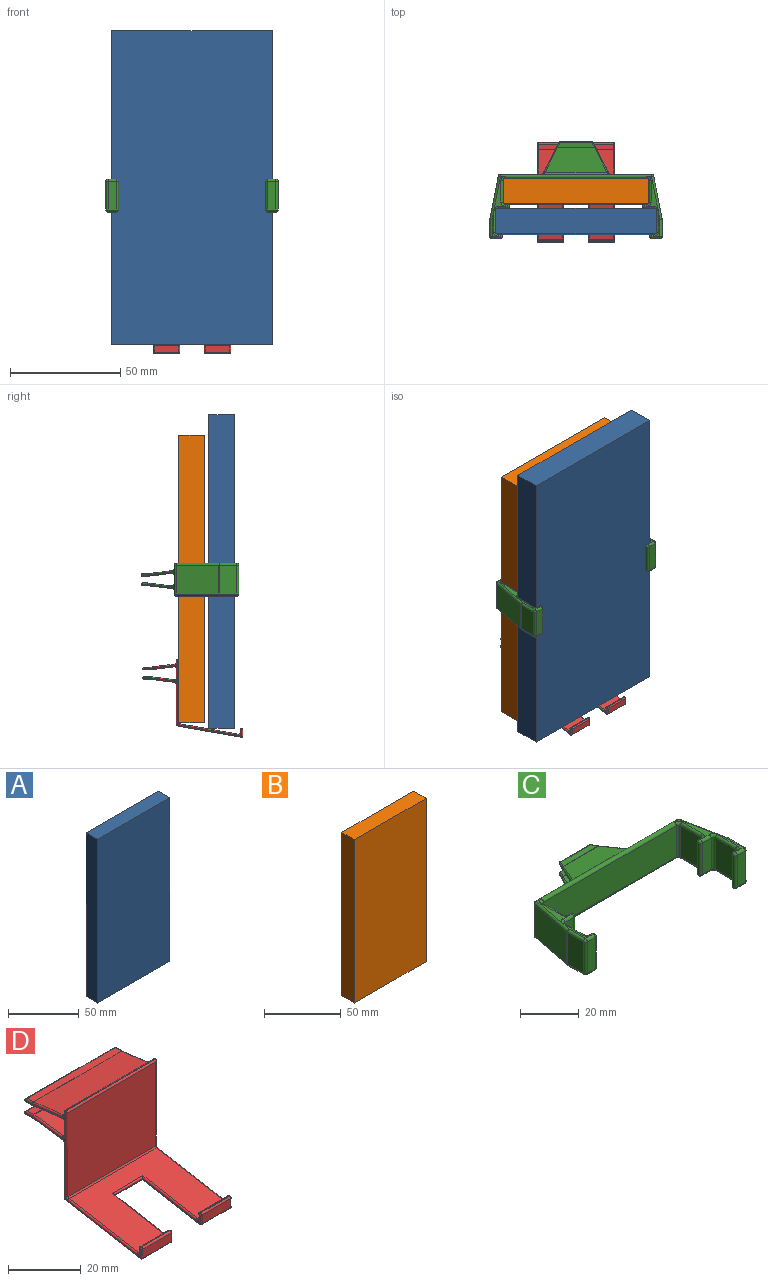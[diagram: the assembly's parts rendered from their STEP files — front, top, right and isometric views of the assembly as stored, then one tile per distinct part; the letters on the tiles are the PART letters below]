
ASSEMBLY  parts=4 mates=3
PART A: 6 faces, bbox 72.5x11.6x142 mm
  f0: plane 72.5x11.6mm, normal (0,0,-1), area 841mm2, adj f1,f3,f4,f5
  f1: plane 142x11.6mm, normal (1,0,0), area 1647.2mm2, adj f0,f2,f4,f5
  f2: plane 72.5x11.6mm, normal (0,0,1), area 841mm2, adj f1,f3,f4,f5
  f3: plane 142x11.6mm, normal (-1,0,0), area 1647.2mm2, adj f0,f2,f4,f5
  f4: plane 142x72.5mm, normal (0,1,0), area 10295mm2, adj f0,f1,f2,f3
  f5: plane 142x72.5mm, normal (0,-1,0), area 10295mm2, adj f0,f1,f2,f3
PART B: 6 faces, bbox 66x11.6x130 mm
  f0: plane 66x11.6mm, normal (0,0,-1), area 765.6mm2, adj f1,f3,f4,f5
  f1: plane 130x11.6mm, normal (1,0,0), area 1508mm2, adj f0,f2,f4,f5
  f2: plane 66x11.6mm, normal (0,0,1), area 765.6mm2, adj f1,f3,f4,f5
  f3: plane 130x11.6mm, normal (-1,0,0), area 1508mm2, adj f0,f2,f4,f5
  f4: plane 130x66mm, normal (0,1,0), area 8580mm2, adj f0,f1,f2,f3
  f5: plane 130x66mm, normal (0,-1,0), area 8580mm2, adj f0,f1,f2,f3
PART C: 188 faces, bbox 78x44.2x15 mm
  f0: plane 11.6x2.75mm, normal (0,0,-1), area 8.1mm2, adj f42,f49,f50,f56,f67
  f1: plane 14.84x5.1mm, normal (0,0,-1), area 22.8mm2, adj f52,f55,f63,f67,f72,f80,f86
  f2: plane 14.84x5.1mm, normal (0,0,-1), area 22.8mm2, adj f86,f91,f99,f100,f101,f106,f112
  f3: plane 11.6x2.75mm, normal (0,0,1), area 8.1mm2, adj f46,f59,f60,f69,f78
  f4: plane 14.84x5.1mm, normal (0,0,1), area 22.8mm2, adj f62,f70,f78,f79,f89,f97,f98
  f5: plane 14.84x5.1mm, normal (0,0,1), area 22.8mm2, adj f97,f110,f111,f115,f116,f118,f119
  f6: plane 14.38x0.2mm, normal (0,1,0), area 2.9mm2, adj f140,f141,f148,f149
  f7: plane 14.38x0.2mm, normal (0,1,0), area 2.9mm2, adj f170,f171,f176,f177
  f8: plane 19.41x13mm, normal (-0.98,0.19,0), area 257.2mm2, adj f91,f95,f96,f110
  f9: plane 13x3.75mm, normal (0,-1,0), area 48.7mm2, adj f65,f66,f75,f83
  f10: plane 11.6x2.75mm, normal (0,0,1), area 8.1mm2, adj f83,f94,f102,f109,f110
  f11: plane 11.6x2.75mm, normal (0,0,-1), area 8.1mm2, adj f65,f81,f82,f91,f92
  f12: plane 27.7x10.85mm, normal (0,-0.12,-0.99), area 243.4mm2, adj f120,f130,f135,f136
  f13: plane 16.85x2.47mm, normal (0,0,-1), area 38.6mm2, adj f134,f135,f141,f142
  f14: plane 16.78x2.39mm, normal (0,0,1), area 37.3mm2, adj f147,f148,f152,f153
  f15: plane 28.07x11.17mm, normal (0,0.12,0.99), area 253.1mm2, adj f123,f146,f152,f155
  f16: plane 16.85x2.47mm, normal (0,0,1), area 38.6mm2, adj f165,f166,f169,f170
  f17: plane 27.7x10.85mm, normal (0,-0.12,0.99), area 243.4mm2, adj f127,f161,f164,f165
  f18: plane 28.07x11.17mm, normal (0,0.12,-0.99), area 253.1mm2, adj f124,f179,f183,f185
  f19: plane 16.78x2.39mm, normal (0,0,-1), area 37.3mm2, adj f177,f178,f182,f183
  f20: plane 68.36x13mm, normal (0,1,0), area 687.2mm2, adj f77,f86,f96,f97,f120,f121,f122,f123
  f21: plane 13x4.25mm, normal (0,-1,0), area 55.2mm2, adj f100,f108,f113,f118
  f22: plane 13x1mm, normal (0,1,0), area 13mm2, adj f100,f113,f117,f118
  f23: plane 13x9.6mm, normal (1,0,0), area 124.8mm2, adj f105,f106,f116,f117
  f24: plane 64x13mm, normal (0,-1,0), area 832mm2, adj f86,f90,f97,f105
  f25: plane 13x9.6mm, normal (-1,0,0), area 124.8mm2, adj f71,f72,f89,f90
  f26: plane 13x1mm, normal (0,1,0), area 13mm2, adj f48,f52,f62,f71
  f27: plane 13x4.25mm, normal (0,-1,0), area 55.2mm2, adj f48,f52,f61,f62
  f28: plane 13x9.6mm, normal (-1,0,0), area 124.8mm2, adj f54,f56,f61,f69
  f29: plane 13x1mm, normal (0,1,0), area 13mm2, adj f41,f42,f46,f54
  f30: plane 13x3.75mm, normal (0,-1,0), area 48.7mm2, adj f41,f42,f45,f46
  f31: plane 19.41x13mm, normal (0.98,0.19,0), area 257.2mm2, adj f58,f67,f77,f78
  f32: plane 13x1mm, normal (0,1,0), area 13mm2, adj f65,f66,f83,f93
  f33: plane 13x9.6mm, normal (1,0,0), area 124.8mm2, adj f92,f93,f108,f109
  f34: plane 14.17x7.09mm, normal (0.89,0.45,0), area 3.3mm2, adj f125,f162,f164,f169,f176,f182,f184,f185
  f35: plane 14.17x7.09mm, normal (-0.89,0.45,0), area 3.3mm2, adj f126,f159,f161,f166,f171,f175,f178,f179
  f36: plane 14.17x7.09mm, normal (0.89,0.45,0), area 3.3mm2, adj f121,f133,f136,f142,f149,f153,f154,f155
  f37: plane 14.17x7.09mm, normal (-0.89,0.45,0), area 3.3mm2, adj f122,f129,f130,f134,f140,f143,f146,f147
  f38: plane 13x7.79mm, normal (-1,0,0), area 101.3mm2, adj f75,f81,f94,f95
  f39: plane 13x7.79mm, normal (1,0,0), area 101.3mm2, adj f45,f50,f58,f59
  f40: sphere r=1mm, area 3.1mm2, adj f41,f42
  f41: cylinder r=1mm len=13mm, axis (0,0,-1), area 40.8mm2, adj f29,f30,f40,f43
  f42: cylinder r=1mm len=3.75mm, axis (1,0,0), area 7.5mm2, adj f0,f29,f30,f40,f44,f49
  f43: sphere r=1mm, area 3.1mm2, adj f41,f46
  f44: sphere r=1mm, area 1.6mm2, adj f42,f45,f50
  f45: cylinder r=1mm len=13mm, axis (0,0,1), area 20.4mm2, adj f30,f39,f44,f51
  f46: cylinder r=1mm len=3.75mm, axis (-1,0,0), area 7.5mm2, adj f3,f29,f30,f43,f51,f60
  f47: sphere r=1mm, area 3.1mm2, adj f48,f52
  f48: cylinder r=1mm len=13mm, axis (0,0,-1), area 40.8mm2, adj f26,f27,f47,f53
  f49: torus R=2mm, axis (0,0,1), area 3.4mm2, adj f0,f42,f54,f56
  f50: cylinder r=1mm len=7.79mm, axis (0,-1,0), area 12.2mm2, adj f0,f39,f44,f57
  f51: sphere r=1mm, area 1.6mm2, adj f45,f46,f59
  f52: cylinder r=1mm len=4.25mm, axis (1,0,0), area 8.2mm2, adj f1,f26,f27,f47,f55,f63
  f53: sphere r=1mm, area 3.1mm2, adj f48,f62
  f54: cylinder r=1mm len=13mm, axis (0,0,1), area 20.4mm2, adj f28,f29,f49,f60
  f55: torus R=2mm, axis (0,0,1), area 3.4mm2, adj f1,f52,f56,f61,f67
  f56: cylinder r=1mm len=9.6mm, axis (0,-1,0), area 15.1mm2, adj f0,f28,f49,f55,f67
  f57: sphere r=1mm, area 0.2mm2, adj f50,f58,f67
  f58: cylinder r=1mm len=13mm, axis (0,0,-1), area 2.5mm2, adj f31,f39,f57,f68
  f59: cylinder r=1mm len=7.79mm, axis (0,1,0), area 12.2mm2, adj f3,f39,f51,f68
  f60: torus R=2mm, axis (0,0,1), area 3.4mm2, adj f3,f46,f54,f69
  f61: cylinder r=1mm len=13mm, axis (0,0,1), area 20.4mm2, adj f27,f28,f55,f70
  f62: cylinder r=1mm len=4.25mm, axis (-1,0,0), area 8.2mm2, adj f4,f26,f27,f53,f70,f79
  f63: torus R=2mm, axis (0,0,1), area 3.4mm2, adj f1,f52,f71,f72
  f64: sphere r=1mm, area 3.1mm2, adj f65,f66
  f65: cylinder r=1mm len=3.75mm, axis (1,0,0), area 7.5mm2, adj f9,f11,f32,f64,f73,f82
  f66: cylinder r=1mm len=13mm, axis (0,0,-1), area 40.8mm2, adj f9,f32,f64,f74
  f67: cylinder r=1mm len=19.6mm, axis (-0.19,0.98,0), area 31.1mm2, adj f0,f1,f31,f55,f56,f57,f76
  f68: sphere r=1mm, area 0.2mm2, adj f58,f59,f78
  f69: cylinder r=1mm len=9.6mm, axis (0,1,0), area 15.1mm2, adj f3,f28,f60,f70,f78
  f70: torus R=2mm, axis (0,0,1), area 3.4mm2, adj f4,f61,f62,f69,f78
  f71: cylinder r=1mm len=13mm, axis (0,0,1), area 20.4mm2, adj f25,f26,f63,f79
  f72: cylinder r=1mm len=9.6mm, axis (0,-1,0), area 15.1mm2, adj f1,f25,f63,f80
  f73: sphere r=1mm, area 1.6mm2, adj f65,f75,f81
  f74: sphere r=1mm, area 3.1mm2, adj f66,f83
  f75: cylinder r=1mm len=13mm, axis (0,0,-1), area 20.4mm2, adj f9,f38,f73,f84
  f76: sphere r=1mm, area 1.4mm2, adj f67,f77,f86
  f77: cylinder r=1mm len=13mm, axis (0,0,1), area 17.9mm2, adj f20,f31,f76,f88
  f78: cylinder r=1mm len=19.6mm, axis (0.19,-0.98,0), area 31.1mm2, adj f3,f4,f31,f68,f69,f70,f88
  f79: torus R=2mm, axis (0,0,1), area 3.4mm2, adj f4,f62,f71,f89
  f80: torus R=2mm, axis (0,0,1), area 3.4mm2, adj f1,f72,f86,f90
  f81: cylinder r=1mm len=7.79mm, axis (0,1,0), area 12.2mm2, adj f11,f38,f73,f85
  f82: torus R=2mm, axis (0,0,1), area 3.4mm2, adj f11,f65,f92,f93
  f83: cylinder r=1mm len=3.75mm, axis (-1,0,0), area 7.5mm2, adj f9,f10,f32,f74,f84,f102
  f84: sphere r=1mm, area 1.6mm2, adj f75,f83,f94
  f85: sphere r=1mm, area 0.2mm2, adj f81,f91,f95
  f86: cylinder r=1mm len=68.36mm, axis (-1,0,0), area 207.9mm2, adj f1,f2,f20,f24,f76,f80,f87,f99
  f87: sphere r=1mm, area 1.4mm2, adj f86,f91,f96
  f88: sphere r=1mm, area 1.4mm2, adj f77,f78,f97
  f89: cylinder r=1mm len=9.6mm, axis (0,1,0), area 15.1mm2, adj f4,f25,f79,f98
  f90: cylinder r=1mm len=13mm, axis (0,0,-1), area 20.4mm2, adj f24,f25,f80,f98
  f91: cylinder r=1mm len=19.6mm, axis (-0.19,-0.98,0), area 31.1mm2, adj f2,f8,f11,f85,f87,f92,f101
  f92: cylinder r=1mm len=9.6mm, axis (0,1,0), area 15.1mm2, adj f11,f33,f82,f91,f101
  f93: cylinder r=1mm len=13mm, axis (0,0,1), area 20.4mm2, adj f32,f33,f82,f102
  f94: cylinder r=1mm len=7.79mm, axis (0,-1,0), area 12.2mm2, adj f10,f38,f84,f103
  f95: cylinder r=1mm len=13mm, axis (0,0,1), area 2.5mm2, adj f8,f38,f85,f103
  f96: cylinder r=1mm len=13mm, axis (0,0,-1), area 17.9mm2, adj f8,f20,f87,f104
  f97: cylinder r=1mm len=68.36mm, axis (1,0,0), area 207.9mm2, adj f4,f5,f20,f24,f88,f98,f104,f111
  f98: torus R=2mm, axis (0,0,1), area 3.4mm2, adj f4,f89,f90,f97
  f99: torus R=2mm, axis (0,0,1), area 3.4mm2, adj f2,f86,f105,f106
  f100: cylinder r=1mm len=4.25mm, axis (1,0,0), area 8.2mm2, adj f2,f21,f22,f101,f107,f112
  f101: torus R=2mm, axis (0,0,1), area 3.4mm2, adj f2,f91,f92,f100,f108
  f102: torus R=2mm, axis (0,0,1), area 3.4mm2, adj f10,f83,f93,f109
  f103: sphere r=1mm, area 0.2mm2, adj f94,f95,f110
  f104: sphere r=1mm, area 1.4mm2, adj f96,f97,f110
  f105: cylinder r=1mm len=13mm, axis (0,0,1), area 20.4mm2, adj f23,f24,f99,f111
  f106: cylinder r=1mm len=9.6mm, axis (0,1,0), area 15.1mm2, adj f2,f23,f99,f112
  f107: sphere r=1mm, area 3.1mm2, adj f100,f113
  f108: cylinder r=1mm len=13mm, axis (0,0,1), area 20.4mm2, adj f21,f33,f101,f115
  f109: cylinder r=1mm len=9.6mm, axis (0,-1,0), area 15.1mm2, adj f10,f33,f102,f110,f115
  f110: cylinder r=1mm len=19.6mm, axis (0.19,0.98,0), area 31.1mm2, adj f5,f8,f10,f103,f104,f109,f115
  f111: torus R=2mm, axis (0,0,1), area 3.4mm2, adj f5,f97,f105,f116
  f112: torus R=2mm, axis (0,0,1), area 3.4mm2, adj f2,f100,f106,f117
  f113: cylinder r=1mm len=13mm, axis (0,0,-1), area 40.8mm2, adj f21,f22,f107,f114
  f114: sphere r=1mm, area 3.1mm2, adj f113,f118
  f115: torus R=2mm, axis (0,0,1), area 3.4mm2, adj f5,f108,f109,f110,f118
  f116: cylinder r=1mm len=9.6mm, axis (0,-1,0), area 15.1mm2, adj f5,f23,f111,f119
  f117: cylinder r=1mm len=13mm, axis (0,0,1), area 20.4mm2, adj f22,f23,f112,f119
  f118: cylinder r=1mm len=4.25mm, axis (-1,0,0), area 8.2mm2, adj f5,f21,f22,f114,f115,f119
  f119: torus R=2mm, axis (0,0,1), area 3.4mm2, adj f5,f116,f117,f118
  f120: cylinder r=1mm len=31.24mm, axis (1,0,0), area 49.5mm2, adj f12,f20,f128,f129,f131,f133
  f121: cylinder r=1mm len=3.23mm, axis (0,0,1), area 1.9mm2, adj f20,f36,f131,f157
  f122: cylinder r=1mm len=3.23mm, axis (0,0,-1), area 1.9mm2, adj f20,f37,f128,f139
  f123: cylinder r=1mm len=31.24mm, axis (1,0,0), area 42.5mm2, adj f15,f20,f139,f143,f156,f157
  f124: cylinder r=1mm len=31.24mm, axis (-1,0,0), area 42.5mm2, adj f18,f20,f172,f175,f186,f187
  f125: cylinder r=1mm len=3.23mm, axis (0,0,-1), area 1.9mm2, adj f20,f34,f160,f187
  f126: cylinder r=1mm len=3.23mm, axis (0,0,1), area 1.9mm2, adj f20,f35,f158,f172
  f127: cylinder r=1mm len=31.24mm, axis (-1,0,0), area 49.5mm2, adj f17,f20,f158,f159,f160,f162
  f128: bspline ~1.4x1.4mm, area 0.6mm2, adj f120,f122,f129
  f129: bspline ~0.88x0.86mm, area 0.6mm2, adj f37,f120,f128,f130
  f130: cylinder r=0.5mm len=11.13mm, axis (0.44,0.89,-0.11), area 9.9mm2, adj f12,f37,f129,f132
  f131: bspline ~1.4x1.4mm, area 0.6mm2, adj f120,f121,f133
  f132: sphere r=0.5mm, area 0mm2, adj f130,f134,f135
  f133: bspline ~0.88x0.86mm, area 0.6mm2, adj f36,f120,f131,f136
  f134: cylinder r=0.5mm len=2.69mm, axis (0.45,0.89,0), area 2.2mm2, adj f13,f37,f132,f137
  f135: cylinder r=0.5mm len=16.85mm, axis (1,0,0), area 1mm2, adj f12,f13,f132,f138
  f136: cylinder r=0.5mm len=11.13mm, axis (0.44,-0.89,0.11), area 9.9mm2, adj f12,f36,f133,f138
  f137: sphere r=0.5mm, area 0.3mm2, adj f134,f140,f141
  f138: sphere r=0.5mm, area 0mm2, adj f135,f136,f142
  f139: bspline ~1.4x1.4mm, area 0.6mm2, adj f122,f123,f143
  f140: cylinder r=0.5mm len=0.45mm, axis (0,0,1), area 0.1mm2, adj f6,f37,f137,f144
  f141: cylinder r=0.5mm len=14.38mm, axis (-1,0,0), area 11.3mm2, adj f6,f13,f137,f145
  f142: cylinder r=0.5mm len=2.69mm, axis (0.45,-0.89,0), area 2.2mm2, adj f13,f36,f138,f145
  f143: bspline ~0.69x0.59mm, area 0.3mm2, adj f37,f123,f139,f146
  f144: sphere r=0.5mm, area 0.3mm2, adj f140,f147,f148
  f145: sphere r=0.5mm, area 0.3mm2, adj f141,f142,f149
  f146: cylinder r=0.5mm len=11.34mm, axis (-0.44,-0.89,0.11), area 9.5mm2, adj f15,f37,f143,f150
  f147: cylinder r=0.5mm len=2.62mm, axis (-0.45,-0.89,0), area 2.1mm2, adj f14,f37,f144,f150
  f148: cylinder r=0.5mm len=14.38mm, axis (1,0,0), area 11.3mm2, adj f6,f14,f144,f151
  f149: cylinder r=0.5mm len=0.45mm, axis (0,0,-1), area 0.1mm2, adj f6,f36,f145,f151
  f150: bspline ~0.58x0.51mm, area 0.1mm2, adj f37,f146,f147,f152
  f151: sphere r=0.5mm, area 0.3mm2, adj f148,f149,f153
  f152: cylinder r=0.5mm len=16.9mm, axis (1,0,0), area 1mm2, adj f14,f15,f150,f154
  f153: cylinder r=0.5mm len=2.62mm, axis (-0.45,0.89,0), area 2.1mm2, adj f14,f36,f151,f154
  f154: bspline ~0.68x0.55mm, area 0.1mm2, adj f36,f152,f153,f155
  f155: cylinder r=0.5mm len=11.34mm, axis (-0.44,0.89,-0.11), area 9.5mm2, adj f15,f36,f154,f156
  f156: bspline ~0.69x0.59mm, area 0.3mm2, adj f36,f123,f155,f157
  f157: bspline ~1.4x1.4mm, area 0.6mm2, adj f121,f123,f156
  f158: bspline ~1.4x1.4mm, area 0.6mm2, adj f126,f127,f159
  f159: bspline ~0.88x0.86mm, area 0.6mm2, adj f35,f127,f158,f161
  f160: bspline ~1.4x1.4mm, area 0.6mm2, adj f125,f127,f162
  f161: cylinder r=0.5mm len=11.13mm, axis (-0.44,-0.89,-0.11), area 9.9mm2, adj f17,f35,f159,f163
  f162: bspline ~0.88x0.86mm, area 0.6mm2, adj f34,f127,f160,f164
  f163: sphere r=0.5mm, area 0mm2, adj f161,f165,f166
  f164: cylinder r=0.5mm len=11.13mm, axis (-0.44,0.89,0.11), area 9.9mm2, adj f17,f34,f162,f167
  f165: cylinder r=0.5mm len=16.85mm, axis (1,0,0), area 1mm2, adj f16,f17,f163,f167
  f166: cylinder r=0.5mm len=2.69mm, axis (-0.45,-0.89,0), area 2.2mm2, adj f16,f35,f163,f168
  f167: sphere r=0.5mm, area 0mm2, adj f164,f165,f169
  f168: sphere r=0.5mm, area 0.3mm2, adj f166,f170,f171
  f169: cylinder r=0.5mm len=2.69mm, axis (-0.45,0.89,0), area 2.2mm2, adj f16,f34,f167,f173
  f170: cylinder r=0.5mm len=14.38mm, axis (-1,0,0), area 11.3mm2, adj f7,f16,f168,f173
  f171: cylinder r=0.5mm len=0.45mm, axis (0,0,-1), area 0.1mm2, adj f7,f35,f168,f174
  f172: bspline ~1.4x1.4mm, area 0.6mm2, adj f124,f126,f175
  f173: sphere r=0.5mm, area 0.3mm2, adj f169,f170,f176
  f174: sphere r=0.5mm, area 0.3mm2, adj f171,f177,f178
  f175: bspline ~0.69x0.59mm, area 0.3mm2, adj f35,f124,f172,f179
  f176: cylinder r=0.5mm len=0.45mm, axis (0,0,1), area 0.1mm2, adj f7,f34,f173,f180
  f177: cylinder r=0.5mm len=14.38mm, axis (1,0,0), area 11.3mm2, adj f7,f19,f174,f180
  f178: cylinder r=0.5mm len=2.62mm, axis (0.45,0.89,0), area 2.1mm2, adj f19,f35,f174,f181
  f179: cylinder r=0.5mm len=11.34mm, axis (0.44,0.89,0.11), area 9.5mm2, adj f18,f35,f175,f181
  f180: sphere r=0.5mm, area 0.3mm2, adj f176,f177,f182
  f181: bspline ~0.57x0.51mm, area 0.1mm2, adj f35,f178,f179,f183
  f182: cylinder r=0.5mm len=2.62mm, axis (0.45,-0.89,0), area 2.1mm2, adj f19,f34,f180,f184
  f183: cylinder r=0.5mm len=16.9mm, axis (1,0,0), area 1mm2, adj f18,f19,f181,f184
  f184: bspline ~0.68x0.55mm, area 0.1mm2, adj f34,f182,f183,f185
  f185: cylinder r=0.5mm len=11.34mm, axis (0.44,-0.89,-0.11), area 9.5mm2, adj f18,f34,f184,f186
  f186: bspline ~0.69x0.59mm, area 0.3mm2, adj f34,f124,f185,f187
  f187: bspline ~1.4x1.4mm, area 0.6mm2, adj f124,f125,f186
PART D: 134 faces, bbox 35x45.2x35.2 mm
  f0: plane 11x1.49mm, normal (0,1,0), area 16.4mm2, adj f82,f90,f91,f95
  f1: plane 11x0.2mm, normal (0,0,1), area 2.2mm2, adj f80,f81,f89,f90
  f2: plane 11x2.9mm, normal (0,-1,0), area 31.9mm2, adj f69,f70,f79,f80
  f3: plane 34x11.61mm, normal (0,0.12,-0.99), area 397.7mm2, adj f31,f32,f38,f39
  f4: plane 34x2.39mm, normal (0,0,-1), area 81.4mm2, adj f28,f30,f32,f33
  f5: plane 35x0.2mm, normal (0,1,0), area 7mm2, adj f23,f24,f30,f99
  f6: plane 34x2.47mm, normal (0,0,1), area 83.9mm2, adj f96,f99,f103,f104
  f7: plane 34x11.41mm, normal (0,-0.12,0.99), area 390.9mm2, adj f102,f103,f113,f114
  f8: plane 34x4.87mm, normal (0,1,0), area 165.5mm2, adj f108,f113,f116,f119
  f9: plane 34x11.41mm, normal (0,-0.12,-0.99), area 390.9mm2, adj f106,f107,f115,f116
  f10: plane 34x2.47mm, normal (0,0,-1), area 83.9mm2, adj f97,f100,f105,f106
  f11: plane 35x0.2mm, normal (0,1,0), area 7mm2, adj f23,f24,f100,f126
  f12: plane 34x2.39mm, normal (0,0,1), area 81.4mm2, adj f122,f126,f129,f130
  f13: plane 34x11.61mm, normal (0,0.12,0.99), area 397.7mm2, adj f121,f128,f129,f133
  f14: plane 34x1.06mm, normal (0,1,0), area 36mm2, adj f120,f123,f127,f128
  f15: plane 35x0.2mm, normal (0,0,1), area 7mm2, adj f23,f24,f64,f123
  f16: plane 34x28.09mm, normal (0,-1,0), area 955.1mm2, adj f57,f64,f71,f72
  f17: plane 34x26.8mm, normal (0,-0.17,0.98), area 667.4mm2, adj f58,f72,f73,f83,f84,f88,f91,f92
  f18: plane 11x1.49mm, normal (0,1,0), area 16.4mm2, adj f59,f60,f73,f74
  f19: plane 11x0.2mm, normal (0,0,1), area 2.2mm2, adj f48,f49,f60,f61
  f20: plane 11x2.9mm, normal (0,-1,0), area 31.9mm2, adj f40,f45,f49,f50
  f21: plane 34x29.2mm, normal (0,0.17,-0.98), area 733.2mm2, adj f36,f45,f46,f55,f56,f62,f68,f69
  f22: plane 34x18.72mm, normal (0,1,0), area 636.5mm2, adj f37,f38,f46,f47
  f23: plane 44.7x34.73mm, normal (1,0,0), area 19.4mm2, adj f5,f11,f15,f28,f29,f31,f34,f36
  f24: plane 44.7x34.73mm, normal (-1,0,0), area 19.4mm2, adj f5,f11,f15,f33,f35,f39,f43,f47
  f25: plane 22.07x4.07mm, normal (-1,0,0), area 4.9mm2, adj f26,f50,f55,f61,f74,f78,f84
  f26: plane 11x0.18mm, normal (0,-0.98,-0.17), area 2mm2, adj f25,f27,f62,f88
  f27: plane 22.07x4.07mm, normal (1,0,0), area 4.9mm2, adj f26,f68,f79,f89,f92,f94,f95
  f28: cylinder r=0.5mm len=2.89mm, axis (0,-1,0), area 2.1mm2, adj f4,f23,f29,f30
  f29: torus R=1mm, axis (1,0,0), area 0.1mm2, adj f23,f28,f31,f32
  f30: cylinder r=0.5mm len=35mm, axis (1,0,0), area 27.2mm2, adj f4,f5,f28,f33
  f31: cylinder r=0.5mm len=11.67mm, axis (0,-0.99,-0.12), area 9.2mm2, adj f3,f23,f29,f34
  f32: cylinder r=0.5mm len=34mm, axis (1,0,0), area 2.1mm2, adj f3,f4,f29,f35
  f33: cylinder r=0.5mm len=2.89mm, axis (0,1,0), area 2.1mm2, adj f4,f24,f30,f35
  f34: torus R=1mm, axis (1,0,0), area 0.8mm2, adj f23,f31,f37,f38
  f35: torus R=1mm, axis (1,0,0), area 0.1mm2, adj f24,f32,f33,f39
  f36: cylinder r=0.5mm len=29.29mm, axis (0,-0.98,-0.17), area 23.3mm2, adj f21,f23,f41,f42
  f37: cylinder r=0.5mm len=18.72mm, axis (0,0,-1), area 14.7mm2, adj f22,f23,f34,f42
  f38: cylinder r=0.5mm len=34mm, axis (1,0,0), area 24.6mm2, adj f3,f22,f34,f43
  f39: cylinder r=0.5mm len=11.67mm, axis (0,0.99,0.12), area 9.2mm2, adj f3,f24,f35,f43
  f40: cylinder r=0.5mm len=2.9mm, axis (0,0,1), area 2.3mm2, adj f20,f23,f41,f44
  f41: sphere r=0.5mm, area 0.4mm2, adj f36,f40,f45
  f42: sphere r=0.5mm, area 0.3mm2, adj f36,f37,f46
  f43: torus R=1mm, axis (1,0,0), area 0.8mm2, adj f24,f38,f39,f47
  f44: sphere r=0.5mm, area 0.4mm2, adj f40,f48,f49
  f45: cylinder r=0.5mm len=11mm, axis (1,0,0), area 9.6mm2, adj f20,f21,f41,f51
  f46: cylinder r=0.5mm len=34mm, axis (-1,0,0), area 23.7mm2, adj f21,f22,f42,f52
  f47: cylinder r=0.5mm len=18.72mm, axis (0,0,1), area 14.7mm2, adj f22,f24,f43,f52
  f48: cylinder r=0.5mm len=0.5mm, axis (0,1,0), area 0.2mm2, adj f19,f23,f44,f53
  f49: cylinder r=0.5mm len=11mm, axis (-1,0,0), area 8.6mm2, adj f19,f20,f44,f54
  f50: cylinder r=0.5mm len=2.9mm, axis (0,0,-1), area 2.3mm2, adj f20,f25,f51,f54
  f51: sphere r=0.5mm, area 0.4mm2, adj f45,f50,f55
  f52: sphere r=0.5mm, area 0.3mm2, adj f46,f47,f56
  f53: sphere r=0.5mm, area 0.4mm2, adj f48,f59,f60
  f54: sphere r=0.5mm, area 0.4mm2, adj f49,f50,f61
  f55: cylinder r=0.5mm len=22.65mm, axis (0,0.98,0.17), area 17.7mm2, adj f21,f25,f51,f62
  f56: cylinder r=0.5mm len=29.29mm, axis (0,0.98,0.17), area 23.3mm2, adj f21,f24,f52,f63
  f57: cylinder r=0.5mm len=28.59mm, axis (0,0,1), area 22.3mm2, adj f16,f23,f64,f65
  f58: cylinder r=0.5mm len=26.89mm, axis (0,0.98,0.17), area 21.4mm2, adj f17,f23,f65,f66
  f59: cylinder r=0.5mm len=1.49mm, axis (0,0,-1), area 1.2mm2, adj f18,f23,f53,f66
  f60: cylinder r=0.5mm len=11mm, axis (-1,0,0), area 8.6mm2, adj f18,f19,f53,f67
  f61: cylinder r=0.5mm len=0.5mm, axis (0,-1,0), area 0.2mm2, adj f19,f25,f54,f67
  f62: cylinder r=0.5mm len=12mm, axis (-1,0,0), area 8.9mm2, adj f21,f26,f55,f68
  f63: sphere r=0.5mm, area 0.4mm2, adj f56,f69,f70
  f64: cylinder r=0.5mm len=35mm, axis (-1,0,0), area 27.2mm2, adj f15,f16,f57,f71
  f65: torus R=1mm, axis (1,0,0), area 0.7mm2, adj f23,f57,f58,f72
  f66: torus R=1mm, axis (1,0,0), area 0.9mm2, adj f23,f58,f59,f73
  f67: sphere r=0.5mm, area 0.4mm2, adj f60,f61,f74
  f68: cylinder r=0.5mm len=22.65mm, axis (0,-0.98,-0.17), area 17.7mm2, adj f21,f27,f62,f75
  f69: cylinder r=0.5mm len=11mm, axis (1,0,0), area 9.6mm2, adj f2,f21,f63,f75
  f70: cylinder r=0.5mm len=2.9mm, axis (0,0,-1), area 2.3mm2, adj f2,f24,f63,f76
  f71: cylinder r=0.5mm len=28.59mm, axis (0,0,-1), area 22.3mm2, adj f16,f24,f64,f77
  f72: cylinder r=0.5mm len=34mm, axis (1,0,0), area 23.7mm2, adj f16,f17,f65,f77
  f73: cylinder r=0.5mm len=11mm, axis (-1,0,0), area 9.6mm2, adj f17,f18,f66,f78
  f74: cylinder r=0.5mm len=1.49mm, axis (0,0,1), area 1.2mm2, adj f18,f25,f67,f78
  f75: sphere r=0.5mm, area 0.4mm2, adj f68,f69,f79
  f76: sphere r=0.5mm, area 0.4mm2, adj f70,f80,f81
  f77: torus R=1mm, axis (1,0,0), area 0.7mm2, adj f24,f71,f72,f83
  f78: torus R=1mm, axis (1,0,0), area 0.9mm2, adj f25,f73,f74,f84
  f79: cylinder r=0.5mm len=2.9mm, axis (0,0,1), area 2.3mm2, adj f2,f27,f75,f85
  f80: cylinder r=0.5mm len=11mm, axis (-1,0,0), area 8.6mm2, adj f1,f2,f76,f85
  f81: cylinder r=0.5mm len=0.5mm, axis (0,-1,0), area 0.2mm2, adj f1,f24,f76,f86
  f82: cylinder r=0.5mm len=1.49mm, axis (0,0,1), area 1.2mm2, adj f0,f24,f86,f87
  f83: cylinder r=0.5mm len=26.89mm, axis (0,-0.98,-0.17), area 21.4mm2, adj f17,f24,f77,f87
  f84: cylinder r=0.5mm len=21.25mm, axis (0,-0.98,-0.17), area 16.6mm2, adj f17,f25,f78,f88
  f85: sphere r=0.5mm, area 0.4mm2, adj f79,f80,f89
  f86: sphere r=0.5mm, area 0.4mm2, adj f81,f82,f90
  f87: torus R=1mm, axis (1,0,0), area 0.9mm2, adj f24,f82,f83,f91
  f88: cylinder r=0.5mm len=12mm, axis (1,0,0), area 8.9mm2, adj f17,f26,f84,f92
  f89: cylinder r=0.5mm len=0.5mm, axis (0,1,0), area 0.2mm2, adj f1,f27,f85,f93
  f90: cylinder r=0.5mm len=11mm, axis (-1,0,0), area 8.6mm2, adj f0,f1,f86,f93
  f91: cylinder r=0.5mm len=11mm, axis (-1,0,0), area 9.6mm2, adj f0,f17,f87,f94
  f92: cylinder r=0.5mm len=21.25mm, axis (0,0.98,0.17), area 16.6mm2, adj f17,f27,f88,f94
  f93: sphere r=0.5mm, area 0.4mm2, adj f89,f90,f95
  f94: torus R=1mm, axis (1,0,0), area 0.9mm2, adj f27,f91,f92,f95
  f95: cylinder r=0.5mm len=1.49mm, axis (0,0,-1), area 1.2mm2, adj f0,f27,f93,f94
  f96: cylinder r=0.5mm len=2.97mm, axis (0,-1,0), area 2.2mm2, adj f6,f24,f98,f99
  f97: cylinder r=0.5mm len=2.97mm, axis (0,1,0), area 2.2mm2, adj f10,f24,f100,f101
  f98: sphere r=0.5mm, area 0mm2, adj f96,f102,f103
  f99: cylinder r=0.5mm len=35mm, axis (-1,0,0), area 27.2mm2, adj f5,f6,f96,f104
  f100: cylinder r=0.5mm len=35mm, axis (-1,0,0), area 27.2mm2, adj f10,f11,f97,f105
  f101: sphere r=0.5mm, area 0mm2, adj f97,f106,f107
  f102: cylinder r=0.5mm len=11.47mm, axis (0,-0.99,-0.12), area 9mm2, adj f7,f24,f98,f109
  f103: cylinder r=0.5mm len=34mm, axis (1,0,0), area 2.1mm2, adj f6,f7,f98,f110
  f104: cylinder r=0.5mm len=2.97mm, axis (0,1,0), area 2.2mm2, adj f6,f23,f99,f110
  f105: cylinder r=0.5mm len=2.97mm, axis (0,-1,0), area 2.2mm2, adj f10,f23,f100,f111
  f106: cylinder r=0.5mm len=34mm, axis (1,0,0), area 2.1mm2, adj f9,f10,f101,f111
  f107: cylinder r=0.5mm len=11.47mm, axis (0,0.99,-0.12), area 9mm2, adj f9,f24,f101,f112
  f108: cylinder r=0.5mm len=4.87mm, axis (0,0,1), area 3.8mm2, adj f8,f24,f109,f112
  f109: torus R=1mm, axis (1,0,0), area 0.9mm2, adj f24,f102,f108,f113
  f110: sphere r=0.5mm, area 0mm2, adj f103,f104,f114
  f111: sphere r=0.5mm, area 0mm2, adj f105,f106,f115
  f112: torus R=1mm, axis (1,0,0), area 0.9mm2, adj f24,f107,f108,f116
  f113: cylinder r=0.5mm len=34mm, axis (1,0,0), area 28.8mm2, adj f7,f8,f109,f117
  f114: cylinder r=0.5mm len=11.47mm, axis (0,0.99,0.12), area 9mm2, adj f7,f23,f110,f117
  f115: cylinder r=0.5mm len=11.47mm, axis (0,-0.99,0.12), area 9mm2, adj f9,f23,f111,f118
  f116: cylinder r=0.5mm len=34mm, axis (-1,0,0), area 28.8mm2, adj f8,f9,f112,f118
  f117: torus R=1mm, axis (1,0,0), area 0.9mm2, adj f23,f113,f114,f119
  f118: torus R=1mm, axis (1,0,0), area 0.9mm2, adj f23,f115,f116,f119
  f119: cylinder r=0.5mm len=4.87mm, axis (0,0,-1), area 3.8mm2, adj f8,f23,f117,f118
  f120: cylinder r=0.5mm len=1.56mm, axis (0,0,1), area 1.1mm2, adj f14,f24,f123,f124
  f121: cylinder r=0.5mm len=11.67mm, axis (0,-0.99,0.12), area 9.2mm2, adj f13,f24,f124,f125
  f122: cylinder r=0.5mm len=2.89mm, axis (0,-1,0), area 2.1mm2, adj f12,f24,f125,f126
  f123: cylinder r=0.5mm len=35mm, axis (-1,0,0), area 27.2mm2, adj f14,f15,f120,f127
  f124: torus R=1mm, axis (1,0,0), area 0.8mm2, adj f24,f120,f121,f128
  f125: torus R=1mm, axis (1,0,0), area 0.1mm2, adj f24,f121,f122,f129
  f126: cylinder r=0.5mm len=35mm, axis (1,0,0), area 27.2mm2, adj f11,f12,f122,f130
  f127: cylinder r=0.5mm len=1.56mm, axis (0,0,-1), area 1.1mm2, adj f14,f23,f123,f131
  f128: cylinder r=0.5mm len=34mm, axis (-1,0,0), area 24.6mm2, adj f13,f14,f124,f131
  f129: cylinder r=0.5mm len=34mm, axis (1,0,0), area 2.1mm2, adj f12,f13,f125,f132
  f130: cylinder r=0.5mm len=2.89mm, axis (0,1,0), area 2.1mm2, adj f12,f23,f126,f132
  f131: torus R=1mm, axis (1,0,0), area 0.8mm2, adj f23,f127,f128,f133
  f132: torus R=1mm, axis (1,0,0), area 0.1mm2, adj f23,f129,f130,f133
  f133: cylinder r=0.5mm len=11.67mm, axis (0,0.99,-0.12), area 9.2mm2, adj f13,f23,f131,f132
PLACE A t=(0,-11.6,3.7)mm
PLACE B t=(0,2,0.3)mm
PLACE C at identity
PLACE D t=(0,23.11,-42.21)mm
MATE planar A.f3 <-> C.f33  axis (-1,0,0) through (-36.25,-5.8,3.7)mm
MATE planar D.f16 <-> B.f4  axis (0,-1,0) through (0,13.6,-50.7)mm
MATE planar B.f4 <-> C.f24  axis (0,1,0) through (0,13.6,0.3)mm
